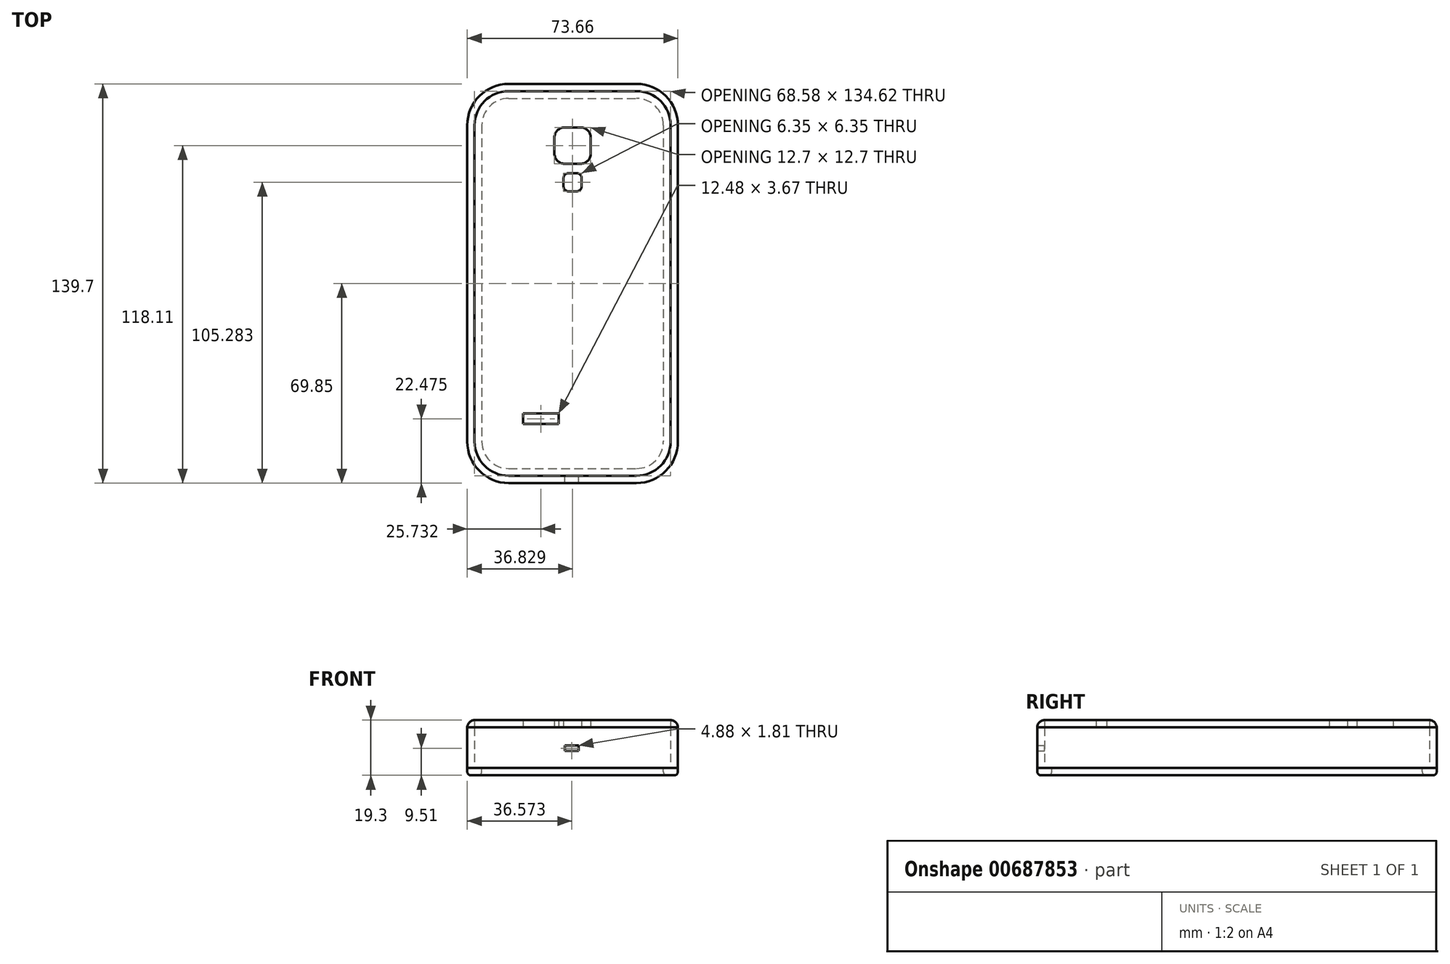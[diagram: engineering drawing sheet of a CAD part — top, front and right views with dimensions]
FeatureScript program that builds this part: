
annotation { "Feature Type Name" : "Feature", "Feature Type Description" : "" }
export const myFeature = defineFeature(function(context is Context, id is Id, definition is map)
    precondition{}
    {
        {
            var Q0;
            Q0=qCreatedBy(makeId("Top.planeOp"),FACE);
            var sketch = newSketch(context, id + "F0", { "sketchPlane" : qUnion([Q0])});
            skLineSegment(sketch, "E0", {"start": v(-21.26, 77.24) * mm, "end": v(23.44, 77.24) * mm});
            skLineSegment(sketch, "E1", {"start": v(35.38, 65.3) * mm, "end": v(35.38, -45.44) * mm});
            skLineSegment(sketch, "E2", {"start": v(-33.2, 65.3) * mm, "end": v(-33.2, -45.44) * mm});
            skLineSegment(sketch, "E3", {"start": v(-21.26, -57.38) * mm, "end": v(23.44, -57.38) * mm});
            skPoint(sketch, "E4.visualSharp", {"position": v(-33.2, 77.24) * mm});
            skArc(sketch, "E4.filletArc", {"start": v(-21.26, 77.24) * mm, "mid": v(-29.7, 73.74) * mm, "end": v(-33.2, 65.3) * mm});
            skPoint(sketch, "E5.visualSharp", {"position": v(35.38, 77.24) * mm});
            skArc(sketch, "E5.filletArc", {"start": v(35.38, 65.3) * mm, "mid": v(31.88, 73.74) * mm, "end": v(23.44, 77.24) * mm});
            skPoint(sketch, "E6.visualSharp", {"position": v(35.38, -57.38) * mm});
            skArc(sketch, "E6.filletArc", {"start": v(23.44, -57.38) * mm, "mid": v(31.88, -53.88) * mm, "end": v(35.38, -45.44) * mm});
            skPoint(sketch, "E7.visualSharp", {"position": v(-33.2, -57.38) * mm});
            skArc(sketch, "E7.filletArc", {"start": v(-33.2, -45.44) * mm, "mid": v(-29.7, -53.88) * mm, "end": v(-21.26, -57.38) * mm});
            skLineSegment(sketch, "E8", {"start": v(1.09, 77.24) * mm, "end": v(1.09, -57.38) * mm});
            skLineSegment(sketch, "E9", {"start": v(1.09, 77.24) * mm, "end": v(1.09, 64.54) * mm});
            skLineSegment(sketch, "E10", {"start": v(1.09, 64.54) * mm, "end": v(-1.7, 64.54) * mm});
            skLineSegment(sketch, "E11", {"start": v(-5.26, 60.98) * mm, "end": v(-5.26, 55.4) * mm});
            skLineSegment(sketch, "E12", {"start": v(-1.7, 51.84) * mm, "end": v(3.88, 51.84) * mm});
            skLineSegment(sketch, "E13", {"start": v(7.44, 55.4) * mm, "end": v(7.44, 60.98) * mm});
            skLineSegment(sketch, "E14", {"start": v(3.88, 64.54) * mm, "end": v(1.09, 64.54) * mm});
            skPoint(sketch, "E15.visualSharp", {"position": v(-5.26, 64.54) * mm});
            skArc(sketch, "E15.filletArc", {"start": v(-1.7, 64.54) * mm, "mid": v(-4.22, 63.5) * mm, "end": v(-5.26, 60.98) * mm});
            skPoint(sketch, "E16.visualSharp", {"position": v(7.44, 64.54) * mm});
            skArc(sketch, "E16.filletArc", {"start": v(7.44, 60.98) * mm, "mid": v(6.4, 63.5) * mm, "end": v(3.88, 64.54) * mm});
            skPoint(sketch, "E17.visualSharp", {"position": v(7.44, 51.84) * mm});
            skArc(sketch, "E17.filletArc", {"start": v(3.88, 51.84) * mm, "mid": v(6.4, 52.88) * mm, "end": v(7.44, 55.4) * mm});
            skPoint(sketch, "E18.visualSharp", {"position": v(-5.26, 51.84) * mm});
            skArc(sketch, "E18.filletArc", {"start": v(-5.26, 55.4) * mm, "mid": v(-4.22, 52.88) * mm, "end": v(-1.7, 51.84) * mm});
            skLineSegment(sketch, "E19", {"start": v(1.09, 51.84) * mm, "end": v(1.09, 48.54) * mm});
            skLineSegment(sketch, "E20", {"start": v(1.09, 48.54) * mm, "end": v(-0.3, 48.54) * mm});
            skLineSegment(sketch, "E21", {"start": v(-2.09, 46.76) * mm, "end": v(-2.09, 43.97) * mm});
            skLineSegment(sketch, "E22", {"start": v(-0.3, 42.19) * mm, "end": v(2.49, 42.19) * mm});
            skLineSegment(sketch, "E23", {"start": v(4.26, 43.97) * mm, "end": v(4.26, 46.76) * mm});
            skLineSegment(sketch, "E24", {"start": v(2.49, 48.54) * mm, "end": v(1.09, 48.54) * mm});
            skPoint(sketch, "E25.visualSharp", {"position": v(-2.09, 48.54) * mm});
            skArc(sketch, "E26.filletArc", {"start": v(-0.3, 48.54) * mm, "mid": v(-1.57, 48.02) * mm, "end": v(-2.09, 46.76) * mm});
            skPoint(sketch, "E27.visualSharp", {"position": v(4.26, 48.54) * mm});
            skArc(sketch, "E27.filletArc", {"start": v(4.26, 46.76) * mm, "mid": v(3.74, 48.02) * mm, "end": v(2.49, 48.54) * mm});
            skPoint(sketch, "E28.visualSharp", {"position": v(4.26, 42.19) * mm});
            skArc(sketch, "E28.filletArc", {"start": v(2.49, 42.19) * mm, "mid": v(3.74, 42.7) * mm, "end": v(4.26, 43.97) * mm});
            skPoint(sketch, "E29.visualSharp", {"position": v(-2.09, 42.19) * mm});
            skArc(sketch, "E29.filletArc", {"start": v(-2.09, 43.97) * mm, "mid": v(-1.57, 42.7) * mm, "end": v(-0.3, 42.19) * mm});
            skLineSegment(sketch, "E30", {"start": v(-5.21, -36.64) * mm, "end": v(-14.67, -36.64) * mm});
            skLineSegment(sketch, "E31", {"start": v(-5.21, -38.17) * mm, "end": v(-14.67, -38.17) * mm});
            skLineSegment(sketch, "E32", {"start": v(-16.25, -37.4) * mm, "end": v(-16.25, -39.28) * mm});
            skLineSegment(sketch, "E33", {"start": v(-16.25, -39.28) * mm, "end": v(-3.77, -39.28) * mm});
            skLineSegment(sketch, "E34", {"start": v(-3.77, -39.28) * mm, "end": v(-3.77, -35.6) * mm});
            skLineSegment(sketch, "E35", {"start": v(-3.77, -35.6) * mm, "end": v(-16.25, -35.6) * mm});
            skLineSegment(sketch, "E36", {"start": v(-16.25, -35.6) * mm, "end": v(-16.25, -37.4) * mm});
            skLineSegment(sketch, "E37.0", {"start": v(37.92, 65.3) * mm, "end": v(37.92, -45.44) * mm});
            skArc(sketch, "E37.1", {"start": v(23.44, -59.92) * mm, "mid": v(33.68, -55.68) * mm, "end": v(37.92, -45.44) * mm});
            skArc(sketch, "E37.2", {"start": v(37.92, 65.3) * mm, "mid": v(33.68, 75.54) * mm, "end": v(23.44, 79.78) * mm});
            skLineSegment(sketch, "E37.3", {"start": v(-21.26, -59.92) * mm, "end": v(23.44, -59.92) * mm});
            skLineSegment(sketch, "E37.4", {"start": v(-21.26, 79.78) * mm, "end": v(23.44, 79.78) * mm});
            skArc(sketch, "E37.5", {"start": v(-21.26, 79.78) * mm, "mid": v(-31.5, 75.54) * mm, "end": v(-35.74, 65.3) * mm});
            skLineSegment(sketch, "E37.6", {"start": v(-35.74, 65.3) * mm, "end": v(-35.74, -45.44) * mm});
            skArc(sketch, "E37.7", {"start": v(-35.74, -45.44) * mm, "mid": v(-31.5, -55.68) * mm, "end": v(-21.26, -59.92) * mm});
            skLineSegment(sketch, "E38.0", {"start": v(-21.26, 74.7) * mm, "end": v(23.44, 74.7) * mm});
            skArc(sketch, "E38.1", {"start": v(32.84, 65.3) * mm, "mid": v(30.09, 71.95) * mm, "end": v(23.44, 74.7) * mm});
            skArc(sketch, "E38.2", {"start": v(-21.26, 74.7) * mm, "mid": v(-27.9, 71.95) * mm, "end": v(-30.66, 65.3) * mm});
            skLineSegment(sketch, "E38.3", {"start": v(32.84, 65.3) * mm, "end": v(32.84, -45.44) * mm});
            skLineSegment(sketch, "E38.4", {"start": v(-30.66, 65.3) * mm, "end": v(-30.66, -45.44) * mm});
            skArc(sketch, "E38.5", {"start": v(-30.66, -45.44) * mm, "mid": v(-27.9, -52.09) * mm, "end": v(-21.26, -54.84) * mm});
            skLineSegment(sketch, "E38.6", {"start": v(-21.26, -54.84) * mm, "end": v(23.44, -54.84) * mm});
            skArc(sketch, "E38.7", {"start": v(23.44, -54.84) * mm, "mid": v(30.09, -52.09) * mm, "end": v(32.84, -45.44) * mm});
            skSolve(sketch);
        }
        {
            var Q0;
            Q0=makeQuery(id+"F0.imprint","IMPRINT",FACE,{"disambiguationData":[TD([[makeQuery(id+"F0.imprint","IMPRINT",EDGE,{"derivedFrom":sQuery(id+"F0.wireOp",EDGE,"E2")}),1.0]])]});
            var Q1;
            Q1=makeQuery(id+"F0.imprint","IMPRINT",FACE,{"disambiguationData":[TD([[makeQuery(id+"F0.imprint","IMPRINT",EDGE,{"derivedFrom":sQuery(id+"F0.wireOp",EDGE,"E1")}),-1.0]])]});
            var Q2;
            Q2=makeQuery(id+"F0.imprint","IMPRINT",FACE,{"disambiguationData":[TD([[makeQuery(id+"F0.imprint","IMPRINT",EDGE,{"derivedFrom":sQuery(id+"F0.wireOp",EDGE,"E13")}),-1.0]])]});
            var Q3;
            {var subQ6=sQuery(id+"F0.wireOp",EDGE,"E10");Q3=makeQuery(id+"F0.imprint","IMPRINT",FACE,{"disambiguationData":[TD([[makeQuery(id+"F0.imprint","IMPRINT",EDGE,{"derivedFrom":subQ6}),-1.0]])]});}
            extrude(context, id + "F1", {"entities" : qUnion([Q0, Q1, Q2, Q3]), "depth" : 14.22 * mm, "offsetDistance" : 25.4 * mm});
        }
        {
            var Q0;
            Q0=makeQuery(id+"F1.opExtrude","SWEPT_FACE",FACE,{"disambiguationData":[OSD([sQuery(id+"F0.wireOp",EDGE,"E2")])]});
            var sketch = newSketch(context, id + "F2", { "sketchPlane" : qUnion([Q0])});
            skLineSegment(sketch, "E39", {"start": v(-36.6, 7.11) * mm, "end": v(-27.2, 7.11) * mm});
            skLineSegment(sketch, "E40", {"start": v(-52.6, 7.11) * mm, "end": v(-17.04, 7.11) * mm});
            skLineSegment(sketch, "E41", {"start": v(-17.04, 7.11) * mm, "end": v(-17.04, 5.77) * mm});
            skLineSegment(sketch, "E42", {"start": v(-17.04, 5.77) * mm, "end": v(-52.6, 5.77) * mm});
            skLineSegment(sketch, "E43", {"start": v(-52.6, 5.77) * mm, "end": v(-52.6, 7.11) * mm});
            skLineSegment(sketch, "E44", {"start": v(-36.6, 7.11) * mm, "end": v(-36.6, 5.77) * mm});
            skLineSegment(sketch, "E45", {"start": v(-36.6, 5.77) * mm, "end": v(-27.2, 5.77) * mm});
            skLineSegment(sketch, "E46", {"start": v(-27.2, 5.77) * mm, "end": v(-27.2, 7.11) * mm});
            skSolve(sketch);
        }
        {
            var Q0;
            Q0 = qSketchRegion(id + "F2", true);
            extrude(context, id + "F3", {"entities" : qUnion([Q0]), "operationType" : NewBodyOperationType.ADD, "oppositeDirection" : true, "depth" : 76.2 * mm, "offsetDistance" : 25.4 * mm});
        }
        {
            var Q0;
            Q0=makeQuery(id+"F1.opExtrude","SWEPT_FACE",FACE,{"disambiguationData":[OSD([sQuery(id+"F0.wireOp",EDGE,"E2")])]});
            var sketch = newSketch(context, id + "F4", { "sketchPlane" : qUnion([Q0])});
            skLineSegment(sketch, "E47", {"start": v(-40.62, 7.11) * mm, "end": v(-40.62, 5.88) * mm});
            skLineSegment(sketch, "E48", {"start": v(-40.62, 5.88) * mm, "end": v(-27.2, 5.88) * mm});
            skLineSegment(sketch, "E49", {"start": v(-27.2, 5.88) * mm, "end": v(-27.2, 7.11) * mm});
            skLineSegment(sketch, "E50", {"start": v(-40.62, 7.11) * mm, "end": v(-27.2, 7.11) * mm});
            skSolve(sketch);
        }
        {
            var Q0;
            Q0=makeQuery(id+"F4.imprint","IMPRINT",FACE,{"disambiguationData":[TD([[makeQuery(id+"F4.imprint","IMPRINT",EDGE,{"derivedFrom":sQuery(id+"F4.wireOp",EDGE,"E47")}),1.0]])]});
            extrude(context, id + "F5", {"entities" : qUnion([Q0]), "operationType" : NewBodyOperationType.ADD, "depth" : 25.4 * mm, "offsetDistance" : 25.4 * mm});
        }
        {
            var Q0;
            Q0=makeQuery(id+"F1.opExtrude","SWEPT_FACE",FACE,{"disambiguationData":[OSD([sQuery(id+"F0.wireOp",EDGE,"E3")])]});
            var sketch = newSketch(context, id + "F6", { "sketchPlane" : qUnion([Q0])});
            skLineSegment(sketch, "E51", {"start": v(-1.6, 7.87) * mm, "end": v(-1.6, 6.07) * mm});
            skLineSegment(sketch, "E52", {"start": v(-1.6, 6.07) * mm, "end": v(3.27, 6.07) * mm});
            skLineSegment(sketch, "E53", {"start": v(3.27, 6.07) * mm, "end": v(3.27, 7.87) * mm});
            skLineSegment(sketch, "E54", {"start": v(3.27, 7.87) * mm, "end": v(-1.6, 7.87) * mm});
            skSolve(sketch);
        }
        {
            var Q0;
            Q0=makeQuery(id+"F0.imprint","IMPRINT",FACE,{"disambiguationData":[TD([[makeQuery(id+"F0.imprint","IMPRINT",EDGE,{"derivedFrom":sQuery(id+"F0.wireOp",EDGE,"E1")}),1.0]])]});
            extrude(context, id + "F7", {"entities" : qUnion([Q0]), "depth" : 14.22 * mm, "offsetDistance" : 25.4 * mm});
        }
        {
            var Q0;
            Q0=makeQuery(id+"F7.opExtrude","CAP_FACE",FACE,{"disambiguationData":[OSD([sQuery(id+"F0.wireOp",EDGE,"E0"),sQuery(id+"F0.wireOp",EDGE,"E1"),sQuery(id+"F0.wireOp",EDGE,"E2"),sQuery(id+"F0.wireOp",EDGE,"E3"),sQuery(id+"F0.wireOp",EDGE,"E4.filletArc"),sQuery(id+"F0.wireOp",EDGE,"E5.filletArc"),sQuery(id+"F0.wireOp",EDGE,"E6.filletArc"),sQuery(id+"F0.wireOp",EDGE,"E7.filletArc"),sQuery(id+"F0.wireOp",EDGE,"E37.0"),sQuery(id+"F0.wireOp",EDGE,"E37.1"),sQuery(id+"F0.wireOp",EDGE,"E37.2"),sQuery(id+"F0.wireOp",EDGE,"E37.3"),sQuery(id+"F0.wireOp",EDGE,"E37.4"),sQuery(id+"F0.wireOp",EDGE,"E37.5"),sQuery(id+"F0.wireOp",EDGE,"E37.6"),sQuery(id+"F0.wireOp",EDGE,"E37.7")])],"isStart":false});
            var Q1;
            Q1=makeQuery(id+"F1.opExtrude","CAP_FACE",FACE,{"disambiguationData":[OSD([sQuery(id+"F0.wireOp",EDGE,"E0"),sQuery(id+"F0.wireOp",EDGE,"E1"),sQuery(id+"F0.wireOp",EDGE,"E2"),sQuery(id+"F0.wireOp",EDGE,"E3"),sQuery(id+"F0.wireOp",EDGE,"E4.filletArc"),sQuery(id+"F0.wireOp",EDGE,"E5.filletArc"),sQuery(id+"F0.wireOp",EDGE,"E6.filletArc"),sQuery(id+"F0.wireOp",EDGE,"E7.filletArc"),sQuery(id+"F0.wireOp",EDGE,"E10"),sQuery(id+"F0.wireOp",EDGE,"E11"),sQuery(id+"F0.wireOp",EDGE,"E12"),sQuery(id+"F0.wireOp",EDGE,"E13"),sQuery(id+"F0.wireOp",EDGE,"E14"),sQuery(id+"F0.wireOp",EDGE,"E15.filletArc"),sQuery(id+"F0.wireOp",EDGE,"E16.filletArc"),sQuery(id+"F0.wireOp",EDGE,"E17.filletArc"),sQuery(id+"F0.wireOp",EDGE,"E18.filletArc"),sQuery(id+"F0.wireOp",EDGE,"E20"),sQuery(id+"F0.wireOp",EDGE,"E21"),sQuery(id+"F0.wireOp",EDGE,"E22"),sQuery(id+"F0.wireOp",EDGE,"E23"),sQuery(id+"F0.wireOp",EDGE,"E24"),sQuery(id+"F0.wireOp",EDGE,"E26.filletArc"),sQuery(id+"F0.wireOp",EDGE,"E27.filletArc"),sQuery(id+"F0.wireOp",EDGE,"E28.filletArc"),sQuery(id+"F0.wireOp",EDGE,"E29.filletArc"),sQuery(id+"F0.wireOp",EDGE,"E32"),sQuery(id+"F0.wireOp",EDGE,"E33"),sQuery(id+"F0.wireOp",EDGE,"E34"),sQuery(id+"F0.wireOp",EDGE,"E35"),sQuery(id+"F0.wireOp",EDGE,"E36")])],"isStart":false});
            extrude(context, id + "F8", {"entities" : qUnion([Q0, Q1]), "depth" : 2.54 * mm, "offsetDistance" : 25.4 * mm});
        }
        {
            var Q0;
            Q0=makeQuery(id+"F0.imprint","IMPRINT",FACE,{"disambiguationData":[TD([[makeQuery(id+"F0.imprint","IMPRINT",EDGE,{"derivedFrom":sQuery(id+"F0.wireOp",EDGE,"E1")}),1.0]])]});
            var Q1;
            Q1=makeQuery(id+"F0.imprint","IMPRINT",FACE,{"disambiguationData":[TD([[makeQuery(id+"F0.imprint","IMPRINT",EDGE,{"derivedFrom":sQuery(id+"F0.wireOp",EDGE,"E1")}),-1.0]])]});
            var Q2;
            Q2=makeQuery(id+"F0.imprint","IMPRINT",FACE,{"disambiguationData":[TD([[makeQuery(id+"F0.imprint","IMPRINT",EDGE,{"derivedFrom":sQuery(id+"F0.wireOp",EDGE,"E2")}),1.0]])]});
            extrude(context, id + "F9", {"entities" : qUnion([Q0, Q1, Q2]), "oppositeDirection" : true, "depth" : 2.54 * mm, "offsetDistance" : 25.4 * mm});
        }
        {
            var Q0;
            Q0=makeQuery(id+"F1.opExtrude","SWEPT_BODY",BODY,{"disambiguationData":[OSD([sQuery(id+"F0.wireOp",EDGE,"E0"),sQuery(id+"F0.wireOp",EDGE,"E1"),sQuery(id+"F0.wireOp",EDGE,"E2"),sQuery(id+"F0.wireOp",EDGE,"E3"),sQuery(id+"F0.wireOp",EDGE,"E4.filletArc"),sQuery(id+"F0.wireOp",EDGE,"E5.filletArc"),sQuery(id+"F0.wireOp",EDGE,"E6.filletArc"),sQuery(id+"F0.wireOp",EDGE,"E7.filletArc"),sQuery(id+"F0.wireOp",EDGE,"E10"),sQuery(id+"F0.wireOp",EDGE,"E11"),sQuery(id+"F0.wireOp",EDGE,"E12"),sQuery(id+"F0.wireOp",EDGE,"E13"),sQuery(id+"F0.wireOp",EDGE,"E14"),sQuery(id+"F0.wireOp",EDGE,"E15.filletArc"),sQuery(id+"F0.wireOp",EDGE,"E16.filletArc"),sQuery(id+"F0.wireOp",EDGE,"E17.filletArc"),sQuery(id+"F0.wireOp",EDGE,"E18.filletArc"),sQuery(id+"F0.wireOp",EDGE,"E20"),sQuery(id+"F0.wireOp",EDGE,"E21"),sQuery(id+"F0.wireOp",EDGE,"E22"),sQuery(id+"F0.wireOp",EDGE,"E23"),sQuery(id+"F0.wireOp",EDGE,"E24"),sQuery(id+"F0.wireOp",EDGE,"E26.filletArc"),sQuery(id+"F0.wireOp",EDGE,"E27.filletArc"),sQuery(id+"F0.wireOp",EDGE,"E28.filletArc"),sQuery(id+"F0.wireOp",EDGE,"E29.filletArc"),sQuery(id+"F0.wireOp",EDGE,"E32"),sQuery(id+"F0.wireOp",EDGE,"E33"),sQuery(id+"F0.wireOp",EDGE,"E34"),sQuery(id+"F0.wireOp",EDGE,"E35"),sQuery(id+"F0.wireOp",EDGE,"E36")])]});
            var Q1;
            Q1=makeQuery(id+"F9.opExtrude","SWEPT_BODY",BODY,{"disambiguationData":[OSD([sQuery(id+"F0.wireOp",EDGE,"E37.0"),sQuery(id+"F0.wireOp",EDGE,"E37.1"),sQuery(id+"F0.wireOp",EDGE,"E37.2"),sQuery(id+"F0.wireOp",EDGE,"E37.3"),sQuery(id+"F0.wireOp",EDGE,"E37.4"),sQuery(id+"F0.wireOp",EDGE,"E37.5"),sQuery(id+"F0.wireOp",EDGE,"E37.6"),sQuery(id+"F0.wireOp",EDGE,"E37.7"),sQuery(id+"F0.wireOp",EDGE,"E38.0"),sQuery(id+"F0.wireOp",EDGE,"E38.1"),sQuery(id+"F0.wireOp",EDGE,"E38.2"),sQuery(id+"F0.wireOp",EDGE,"E38.3"),sQuery(id+"F0.wireOp",EDGE,"E38.4"),sQuery(id+"F0.wireOp",EDGE,"E38.5"),sQuery(id+"F0.wireOp",EDGE,"E38.6"),sQuery(id+"F0.wireOp",EDGE,"E38.7")])]});
            booleanBodies(context, id + "F10", {"operationType" : BooleanOperationType.SUBTRACTION, "tools" : qUnion([Q0]), "targets" : qUnion([Q1])});
        }
        {
            var Q0;
            Q0=makeQuery(id+"F9.opExtrude","CAP_EDGE",EDGE,{"disambiguationData":[OSD([sQuery(id+"F0.wireOp",EDGE,"E38.4")])],"isStart":false});
            var Q1;
            Q1=makeQuery(id+"F9.opExtrude","CAP_EDGE",EDGE,{"disambiguationData":[OSD([sQuery(id+"F0.wireOp",EDGE,"E37.6")])],"isStart":false});
            fillet(context, id + "F11", {"entities" : qUnion([Q0, Q1]), "radius" : 1.27 * mm, "tangentPropagation" : true, "allowEdgeOverflow" : false});
        }
        {
            var Q0;
            Q0=makeQuery(id+"F6.imprint","IMPRINT",FACE,{"disambiguationData":[TD([[makeQuery(id+"F6.imprint","IMPRINT",EDGE,{"derivedFrom":sQuery(id+"F6.wireOp",EDGE,"E51")}),1.0]])]});
            extrude(context, id + "F12", {"entities" : qUnion([Q0]), "operationType" : NewBodyOperationType.REMOVE, "depth" : 14.38 * mm, "offsetDistance" : 25.4 * mm, "symmetric" : true});
        }
        {
            var Q0;
            Q0=makeQuery(id+"F8.opExtrude","CAP_EDGE",EDGE,{"disambiguationData":[OSD([sQuery(id+"F0.wireOp",EDGE,"E37.0")])],"isStart":false});
            fillet(context, id + "F13", {"entities" : qUnion([Q0]), "radius" : 2.54 * mm, "tangentPropagation" : true, "allowEdgeOverflow" : false});
        }
    });
